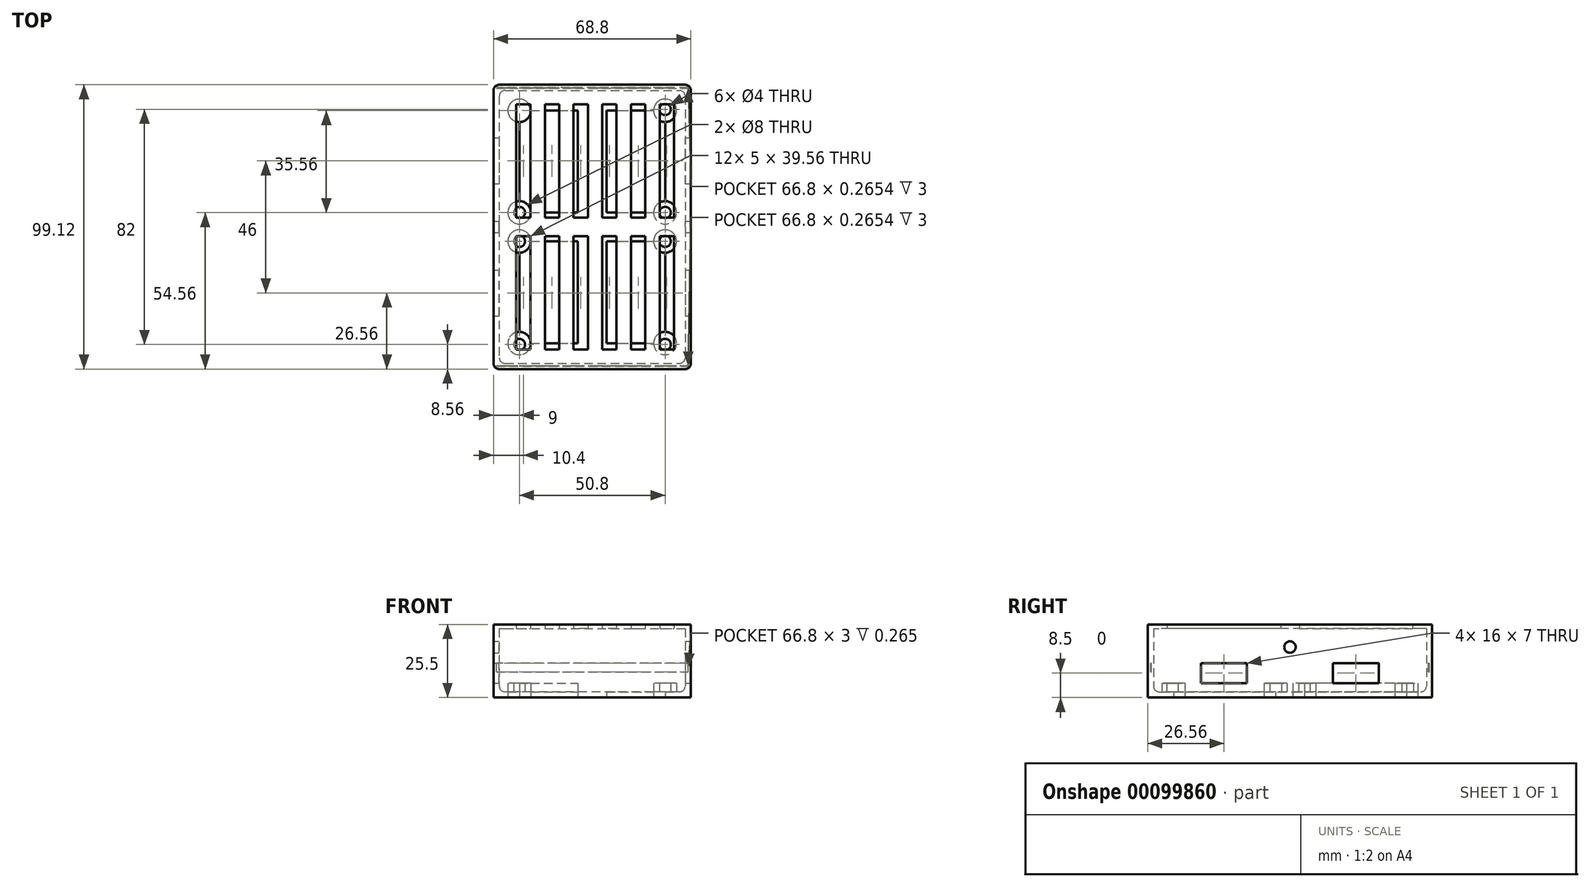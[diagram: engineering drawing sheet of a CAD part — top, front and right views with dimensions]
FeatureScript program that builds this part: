
annotation { "Feature Type Name" : "Feature", "Feature Type Description" : "" }
export const myFeature = defineFeature(function(context is Context, id is Id, definition is map)
    precondition{}
    {
        {
            var Q0;
            Q0=qCreatedBy(makeId("Top.planeOp"),FACE);
            var sketch = newSketch(context, id + "F0", { "sketchPlane" : qUnion([Q0])});
            skLineSegment(sketch, "E0.top", {"start": v(-32.4, -24.56) * mm, "end": v(32.4, -24.56) * mm});
            skLineSegment(sketch, "E0.left", {"start": v(-32.4, 24.56) * mm, "end": v(-32.4, -24.56) * mm});
            skLineSegment(sketch, "E0.right", {"start": v(32.4, 24.56) * mm, "end": v(32.4, -24.56) * mm});
            skPoint(sketch, "E0.middle", {"position": v(0, 0) * mm});
            skCircle(sketch, "E1", {"center": v(-25.4, 18) * mm, "radius": 4 * mm});
            skCircle(sketch, "E2", {"center": v(-25.4, -17.56) * mm, "radius": 4 * mm});
            skCircle(sketch, "E3", {"center": v(-25.4, 18) * mm, "radius": 2 * mm});
            skCircle(sketch, "E4", {"center": v(25.4, 18) * mm, "radius": 4 * mm});
            skCircle(sketch, "E5.MirrorC", {"center": v(-25.4, -18) * mm, "radius": 2 * mm});
            skCircle(sketch, "E6.MirrorC", {"center": v(25.4, 18) * mm, "radius": 2 * mm});
            skCircle(sketch, "E7.MirrorC", {"center": v(25.4, -18) * mm, "radius": 2 * mm});
            skCircle(sketch, "E8.MirrorC", {"center": v(25.4, -17.56) * mm, "radius": 4 * mm});
            skLineSegment(sketch, "E9.top", {"start": v(-34.4, -26.56) * mm, "end": v(34.4, -26.56) * mm});
            skLineSegment(sketch, "E9.left", {"start": v(-34.4, 26.56) * mm, "end": v(-34.4, -26.56) * mm});
            skLineSegment(sketch, "E9.right", {"start": v(34.4, 26.56) * mm, "end": v(34.4, -26.56) * mm});
            skLineSegment(sketch, "E10.bottom", {"start": v(-31, 23) * mm, "end": v(31, 23) * mm, "construction": true});
            skLineSegment(sketch, "E10.top", {"start": v(-31, -23) * mm, "end": v(31, -23) * mm, "construction": true});
            skLineSegment(sketch, "E10.left", {"start": v(-31, 23) * mm, "end": v(-31, -23) * mm, "construction": true});
            skLineSegment(sketch, "E10.right", {"start": v(31, 23) * mm, "end": v(31, -23) * mm, "construction": true});
            skLineSegment(sketch, "E11.MirrorCS", {"start": v(-31, 69) * mm, "end": v(31, 69) * mm, "construction": true});
            skLineSegment(sketch, "E12", {"start": v(-31, 69) * mm, "end": v(-31, 23) * mm, "construction": true});
            skLineSegment(sketch, "E13", {"start": v(31, 69) * mm, "end": v(31, 23) * mm, "construction": true});
            skLineSegment(sketch, "E14.MirrorCS", {"start": v(-32.4, 70.56) * mm, "end": v(32.4, 70.56) * mm});
            skLineSegment(sketch, "E15.MirrorCS", {"start": v(-34.4, 72.56) * mm, "end": v(34.4, 72.56) * mm});
            skLineSegment(sketch, "E16", {"start": v(-32.4, 70.56) * mm, "end": v(-32.4, 24.56) * mm});
            skLineSegment(sketch, "E17", {"start": v(-34.4, 26.56) * mm, "end": v(-34.4, 72.56) * mm});
            skLineSegment(sketch, "E18", {"start": v(32.4, 24.56) * mm, "end": v(32.4, 70.56) * mm});
            skLineSegment(sketch, "E19", {"start": v(34.4, 72.56) * mm, "end": v(34.4, 26.56) * mm});
            skCircle(sketch, "E20.MirrorC", {"center": v(-25.4, 28) * mm, "radius": 2 * mm});
            skCircle(sketch, "E21.MirrorC", {"center": v(-25.4, 28) * mm, "radius": 4 * mm});
            skCircle(sketch, "E22.MirrorC", {"center": v(25.4, 28) * mm, "radius": 2 * mm});
            skCircle(sketch, "E23.MirrorC", {"center": v(25.4, 28) * mm, "radius": 4 * mm});
            skCircle(sketch, "E24.MirrorC", {"center": v(25.4, 63.56) * mm, "radius": 4 * mm});
            skCircle(sketch, "E25.MirrorC", {"center": v(25.4, 64) * mm, "radius": 2 * mm});
            skCircle(sketch, "E26.MirrorC", {"center": v(-25.4, 63.56) * mm, "radius": 4 * mm});
            skCircle(sketch, "E27.MirrorC", {"center": v(-25.4, 64) * mm, "radius": 2 * mm});
            skLineSegment(sketch, "E28.bottom", {"start": v(-25.4, 59.56) * mm, "end": v(25.4, 59.56) * mm, "construction": true});
            skLineSegment(sketch, "E28.top", {"start": v(-25.4, -13.56) * mm, "end": v(25.4, -13.56) * mm, "construction": true});
            skLineSegment(sketch, "E28.left", {"start": v(-25.4, 59.56) * mm, "end": v(-25.4, -13.56) * mm, "construction": true});
            skLineSegment(sketch, "E28.right", {"start": v(25.4, 59.56) * mm, "end": v(25.4, -13.56) * mm, "construction": true});
            skPoint(sketch, "E29", {"position": v(0, 23) * mm});
            skLineSegment(sketch, "E30.bottom", {"start": v(-25.4, 28) * mm, "end": v(-23.4, 28) * mm});
            skLineSegment(sketch, "E30.top", {"start": v(-25.4, 18) * mm, "end": v(-5, 18) * mm});
            skLineSegment(sketch, "E30.left", {"start": v(-25.4, 28) * mm, "end": v(-25.4, 18) * mm});
            skLineSegment(sketch, "E30.right", {"start": v(25.4, 28) * mm, "end": v(25.4, 18) * mm});
            skLineSegment(sketch, "E31.bottom", {"start": v(-25.4, 63.56) * mm, "end": v(-5, 63.56) * mm});
            skLineSegment(sketch, "E31.top", {"start": v(-25.4, -17.56) * mm, "end": v(-5, -17.56) * mm});
            skLineSegment(sketch, "E31.left", {"start": v(-25.4, 63.56) * mm, "end": v(-25.4, 32) * mm});
            skLineSegment(sketch, "E31.right", {"start": v(25.4, 63.56) * mm, "end": v(25.4, -17.56) * mm});
            skLineSegment(sketch, "E32.left", {"start": v(-5, 63.56) * mm, "end": v(-5, 28) * mm});
            skLineSegment(sketch, "E32.right", {"start": v(5, 63.56) * mm, "end": v(5, 28) * mm});
            skLineSegment(sketch, "E33.trimOffspring", {"start": v(5, 63.56) * mm, "end": v(25.4, 63.56) * mm});
            skLineSegment(sketch, "E34.trimOffspring", {"start": v(5, 28) * mm, "end": v(25.4, 28) * mm});
            skLineSegment(sketch, "E35.trimOffspring", {"start": v(-5, 18) * mm, "end": v(-5, -17.56) * mm});
            skLineSegment(sketch, "E36.trimOffspring", {"start": v(5, 18) * mm, "end": v(5, -17.56) * mm});
            skLineSegment(sketch, "E37.trimOffspring", {"start": v(5, 18) * mm, "end": v(25.4, 18) * mm});
            skLineSegment(sketch, "E38.trimOffspring", {"start": v(5, -17.56) * mm, "end": v(25.4, -17.56) * mm});
            skLineSegment(sketch, "E39.trimOffspring", {"start": v(-25.4, 28) * mm, "end": v(-25.4, -17.56) * mm});
            skLineSegment(sketch, "E40.trimOffspring", {"start": v(-21.4, 28) * mm, "end": v(-5, 28) * mm});
            skSolve(sketch);
        }
        {
            var Q0;
            Q0 = qSketchRegion(id + "F0", true);
            var Q1;
            Q1=makeQuery(id+"F0.imprint","IMPRINT",FACE,{"disambiguationData":[TD([[makeQuery(id+"F0.imprint","IMPRINT",EDGE,{"derivedFrom":sQuery(id+"F0.wireOp",EDGE,"E0.top")}),1.0]])]});
            extrude(context, id + "F1", {"entities" : qUnion([Q0, Q1]), "depth" : 2 * mm});
        }
        {
            var Q0;
            Q0=makeQuery(id+"F0.imprint","IMPRINT",FACE,{"disambiguationData":[TD([[makeQuery(id+"F0.imprint","IMPRINT",EDGE,{"derivedFrom":sQuery(id+"F0.wireOp",EDGE,"E1")}),1.0]])]});
            var Q1;
            Q1=makeQuery(id+"F0.imprint","IMPRINT",FACE,{"disambiguationData":[TD([[makeQuery(id+"F0.imprint","IMPRINT",EDGE,{"derivedFrom":sQuery(id+"F0.wireOp",EDGE,"E4")}),1.0]])]});
            var Q2;
            Q2=makeQuery(id+"F0.imprint","IMPRINT",FACE,{"disambiguationData":[TD([[makeQuery(id+"F0.imprint","IMPRINT",EDGE,{"derivedFrom":sQuery(id+"F0.wireOp",EDGE,"E7.MirrorC")}),-1.0]])]});
            var Q3;
            Q3=makeQuery(id+"F0.imprint","IMPRINT",FACE,{"disambiguationData":[TD([[makeQuery(id+"F0.imprint","IMPRINT",EDGE,{"derivedFrom":sQuery(id+"F0.wireOp",EDGE,"E2")}),1.0]])]});
            var Q4;
            Q4=makeQuery(id+"F0.imprint","IMPRINT",FACE,{"disambiguationData":[TD([[makeQuery(id+"F0.imprint","IMPRINT",EDGE,{"derivedFrom":sQuery(id+"F0.wireOp",EDGE,"E20.MirrorC")}),1.0]])]});
            var Q5;
            Q5=makeQuery(id+"F0.imprint","IMPRINT",FACE,{"disambiguationData":[TD([[makeQuery(id+"F0.imprint","IMPRINT",EDGE,{"derivedFrom":sQuery(id+"F0.wireOp",EDGE,"E26.MirrorC")}),-1.0]])]});
            var Q6;
            Q6=makeQuery(id+"F0.imprint","IMPRINT",FACE,{"disambiguationData":[TD([[makeQuery(id+"F0.imprint","IMPRINT",EDGE,{"derivedFrom":sQuery(id+"F0.wireOp",EDGE,"E24.MirrorC")}),1.0]])]});
            var Q7;
            Q7=makeQuery(id+"F0.imprint","IMPRINT",FACE,{"disambiguationData":[TD([[makeQuery(id+"F0.imprint","IMPRINT",EDGE,{"derivedFrom":sQuery(id+"F0.wireOp",EDGE,"E22.MirrorC")}),-1.0]])]});
            extrude(context, id + "F2", {"entities" : qUnion([Q0, Q1, Q2, Q3, Q4, Q5, Q6, Q7]), "operationType" : NewBodyOperationType.ADD, "depth" : 5 * mm});
        }
        {
            var Q0;
            Q0=makeQuery(id+"F0.imprint","IMPRINT",FACE,{"disambiguationData":[TD([[makeQuery(id+"F0.imprint","IMPRINT",EDGE,{"derivedFrom":sQuery(id+"F0.wireOp",EDGE,"E0.top")}),-1.0]])]});
            extrude(context, id + "F3", {"entities" : qUnion([Q0]), "operationType" : NewBodyOperationType.ADD, "depth" : 12 * mm});
        }
        {
            var Q0;
            Q0=makeQuery(id+"F3.opExtrude","CAP_FACE",FACE,{"disambiguationData":[OSD([sQuery(id+"F0.wireOp",EDGE,"E0.bottom"),sQuery(id+"F0.wireOp",EDGE,"E0.top"),sQuery(id+"F0.wireOp",EDGE,"E0.left"),sQuery(id+"F0.wireOp",EDGE,"E0.right"),sQuery(id+"F0.wireOp",EDGE,"E9.bottom"),sQuery(id+"F0.wireOp",EDGE,"E9.top"),sQuery(id+"F0.wireOp",EDGE,"E9.left"),sQuery(id+"F0.wireOp",EDGE,"E9.right")])],"isStart":false});
            var sketch = newSketch(context, id + "F4", { "sketchPlane" : qUnion([Q0])});
            skLineSegment(sketch, "E41.top", {"start": v(-33.4, -25.3) * mm, "end": v(33.4, -25.3) * mm});
            skLineSegment(sketch, "E41.left", {"start": v(-33.4, 25.3) * mm, "end": v(-33.4, -25.3) * mm});
            skLineSegment(sketch, "E41.right", {"start": v(33.4, 25.3) * mm, "end": v(33.4, -25.3) * mm});
            skPoint(sketch, "E41.middle", {"position": v(0, 0) * mm});
            skLineSegment(sketch, "E42.0", {"start": v(-34.4, -26.56) * mm, "end": v(-34.4, -26.56) * mm});
            skLineSegment(sketch, "E43.0", {"start": v(-34.4, -26.56) * mm, "end": v(34.4, -26.56) * mm});
            skLineSegment(sketch, "E44.0", {"start": v(34.4, -26.56) * mm, "end": v(34.4, -26.56) * mm});
            skLineSegment(sketch, "E45.0", {"start": v(-31, 23) * mm, "end": v(31, 23) * mm, "construction": true});
            skLineSegment(sketch, "E46.MirrorCS", {"start": v(-33.4, 71.3) * mm, "end": v(33.4, 71.3) * mm});
            skLineSegment(sketch, "E47.MirrorCS", {"start": v(-34.4, 72.56) * mm, "end": v(34.4, 72.56) * mm});
            skLineSegment(sketch, "E48.MirrorCS", {"start": v(33.4, 20.7) * mm, "end": v(33.4, 71.3) * mm});
            skLineSegment(sketch, "E49.MirrorCS", {"start": v(-33.4, 20.7) * mm, "end": v(-33.4, 71.3) * mm});
            skLineSegment(sketch, "E50.0", {"start": v(-34.4, 26.56) * mm, "end": v(-34.4, 72.56) * mm});
            skLineSegment(sketch, "E51.0", {"start": v(-34.4, 26.56) * mm, "end": v(-34.4, -26.56) * mm});
            skLineSegment(sketch, "E52.0", {"start": v(34.4, 72.56) * mm, "end": v(34.4, 26.56) * mm});
            skLineSegment(sketch, "E53.0", {"start": v(34.4, 26.56) * mm, "end": v(34.4, -26.56) * mm});
            skPoint(sketch, "E54.MirrorCS.end.orphan", {"position": v(30.4, 68.78) * mm});
            skPoint(sketch, "E54.MirrorCS.start.orphan", {"position": v(-30.4, 68.78) * mm});
            skPoint(sketch, "E55.MirrorCS.start.orphan", {"position": v(-30.4, 23.22) * mm});
            skPoint(sketch, "E56.0.1.start.orphan", {"position": v(-30.4, 22.78) * mm});
            skPoint(sketch, "E56.0.2.start.orphan", {"position": v(-30.4, -22.78) * mm});
            skPoint(sketch, "E56.0.3.end.orphan", {"position": v(30.4, 22.78) * mm});
            skPoint(sketch, "E56.0.3.start.orphan", {"position": v(30.4, -22.78) * mm});
            skPoint(sketch, "E57.MirrorCS.end.orphan", {"position": v(30.4, 23.22) * mm});
            skSolve(sketch);
        }
        {
            var Q0;
            Q0 = qSketchRegion(id + "F4", true);
            extrude(context, id + "F5", {"entities" : qUnion([Q0]), "operationType" : NewBodyOperationType.REMOVE, "oppositeDirection" : true, "depth" : 3 * mm});
        }
        {
            var Q0;
            Q0=makeQuery(id+"F5.boolean.opBoolean","COPY",FACE,{"derivedFrom":makeQuery(id+"F5.opExtrude","CAP_FACE",FACE,{"disambiguationData":[OSD([sQuery(id+"F4.wireOp",EDGE,"E41.top"),sQuery(id+"F4.wireOp",EDGE,"E41.left"),sQuery(id+"F4.wireOp",EDGE,"E41.right"),sQuery(id+"F4.wireOp",EDGE,"E43.0"),sQuery(id+"F4.wireOp",EDGE,"E46.MirrorCS"),sQuery(id+"F4.wireOp",EDGE,"E47.MirrorCS"),sQuery(id+"F4.wireOp",EDGE,"E48.MirrorCS"),sQuery(id+"F4.wireOp",EDGE,"E49.MirrorCS"),sQuery(id+"F4.wireOp",EDGE,"E50.0"),sQuery(id+"F4.wireOp",EDGE,"E51.0"),sQuery(id+"F4.wireOp",EDGE,"E52.0"),sQuery(id+"F4.wireOp",EDGE,"E53.0")])],"isStart":false})});
            cPlane(context, id + "F6", {"entities" : qUnion([Q0]), "cplaneType" : CPlaneType.OFFSET, "offset" : 15 * mm, "width" : 150 * mm, "height" : 150 * mm});
        }
        {
            var Q0;
            Q0=qCreatedBy(id+"F6.planeOp",FACE);
            var sketch = newSketch(context, id + "F7", { "sketchPlane" : qUnion([Q0])});
            skLineSegment(sketch, "E58.left", {"start": v(-26.5, 19.78) * mm, "end": v(-26.5, -19.78) * mm});
            skLineSegment(sketch, "E59", {"start": v(-26.5, 19.78) * mm, "end": v(-21.5, 19.78) * mm});
            skLineSegment(sketch, "E60", {"start": v(-21.5, 19.78) * mm, "end": v(-21.5, -19.78) * mm});
            skLineSegment(sketch, "E61", {"start": v(-26.5, -19.78) * mm, "end": v(-21.5, -19.78) * mm});
            skLineSegment(sketch, "E62.left", {"start": v(-16.5, 19.78) * mm, "end": v(-16.5, -19.78) * mm});
            skLineSegment(sketch, "E63", {"start": v(-16.5, 19.78) * mm, "end": v(-11.5, 19.78) * mm});
            skLineSegment(sketch, "E64", {"start": v(-11.5, 19.78) * mm, "end": v(-11.5, -19.78) * mm});
            skLineSegment(sketch, "E65", {"start": v(-16.5, -19.78) * mm, "end": v(-11.5, -19.78) * mm});
            skLineSegment(sketch, "E66", {"start": v(-9, 22.94) * mm, "end": v(-9, -17.5) * mm, "construction": true});
            skLineSegment(sketch, "E67.MirrorCS", {"start": v(8.5, 19.78) * mm, "end": v(3.5, 19.78) * mm});
            skLineSegment(sketch, "E68.MirrorCS", {"start": v(8.5, 19.78) * mm, "end": v(8.5, -19.78) * mm});
            skLineSegment(sketch, "E69.MirrorCS", {"start": v(3.5, 19.78) * mm, "end": v(3.5, -19.78) * mm});
            skLineSegment(sketch, "E70.MirrorCS", {"start": v(-1.5, 19.78) * mm, "end": v(-1.5, -19.78) * mm});
            skLineSegment(sketch, "E71.MirrorCS", {"start": v(-1.5, 19.78) * mm, "end": v(-6.5, 19.78) * mm});
            skLineSegment(sketch, "E72.MirrorCS", {"start": v(-1.5, -19.78) * mm, "end": v(-6.5, -19.78) * mm});
            skLineSegment(sketch, "E73.MirrorCS", {"start": v(8.5, -19.78) * mm, "end": v(3.5, -19.78) * mm});
            skLineSegment(sketch, "E74.MirrorCS", {"start": v(-6.5, 19.78) * mm, "end": v(-6.5, -19.78) * mm});
            skLineSegment(sketch, "E75", {"start": v(11, 21.68) * mm, "end": v(11, -19.6) * mm, "construction": true});
            skLineSegment(sketch, "E76.MirrorCS", {"start": v(23.5, 19.78) * mm, "end": v(28.5, 19.78) * mm});
            skLineSegment(sketch, "E77.MirrorCS", {"start": v(18.5, 19.78) * mm, "end": v(18.5, -19.78) * mm});
            skLineSegment(sketch, "E78.MirrorCS", {"start": v(23.5, 19.78) * mm, "end": v(23.5, -19.78) * mm});
            skLineSegment(sketch, "E79.MirrorCS", {"start": v(23.5, -19.78) * mm, "end": v(28.5, -19.78) * mm});
            skLineSegment(sketch, "E80.MirrorCS", {"start": v(13.5, -19.78) * mm, "end": v(18.5, -19.78) * mm});
            skLineSegment(sketch, "E81.MirrorCS", {"start": v(13.5, 19.78) * mm, "end": v(13.5, -19.78) * mm});
            skLineSegment(sketch, "E82.MirrorCS", {"start": v(13.5, 19.78) * mm, "end": v(18.5, 19.78) * mm});
            skLineSegment(sketch, "E83.MirrorCS", {"start": v(28.5, 19.78) * mm, "end": v(28.5, -19.78) * mm});
            skLineSegment(sketch, "E84", {"start": v(31, 21.5) * mm, "end": v(31, -15.9) * mm, "construction": true});
            skLineSegment(sketch, "E85.0", {"start": v(-32.4, -24.56) * mm, "end": v(32.4, -24.56) * mm});
            skLineSegment(sketch, "E86.0", {"start": v(-32.4, 24.56) * mm, "end": v(-32.4, -24.56) * mm});
            skLineSegment(sketch, "E87", {"start": v(32.4, -24.56) * mm, "end": v(32.4, 21) * mm});
            skLineSegment(sketch, "E88.0", {"start": v(-34.4, 26.56) * mm, "end": v(-34.4, -26.56) * mm});
            skLineSegment(sketch, "E89.0", {"start": v(34.4, 26.56) * mm, "end": v(34.4, -26.56) * mm});
            skLineSegment(sketch, "E90.0", {"start": v(-34.4, -26.56) * mm, "end": v(34.4, -26.56) * mm});
            skLineSegment(sketch, "E91.0", {"start": v(33.4, 23.78) * mm, "end": v(33.4, -25.3) * mm});
            skLineSegment(sketch, "E92.MirrorCS", {"start": v(13.5, 65.78) * mm, "end": v(18.5, 65.78) * mm});
            skLineSegment(sketch, "E93.MirrorCS", {"start": v(23.5, 26.22) * mm, "end": v(28.5, 26.22) * mm});
            skLineSegment(sketch, "E94.MirrorCS", {"start": v(13.5, 26.22) * mm, "end": v(18.5, 26.22) * mm});
            skLineSegment(sketch, "E95.MirrorCS", {"start": v(-16.5, 65.78) * mm, "end": v(-11.5, 65.78) * mm});
            skLineSegment(sketch, "E96.MirrorCS", {"start": v(-26.5, 65.78) * mm, "end": v(-21.5, 65.78) * mm});
            skLineSegment(sketch, "E97.MirrorCS", {"start": v(-1.5, 65.78) * mm, "end": v(-6.5, 65.78) * mm});
            skLineSegment(sketch, "E98.MirrorCS", {"start": v(-1.5, 26.22) * mm, "end": v(-6.5, 26.22) * mm});
            skLineSegment(sketch, "E99.MirrorCS", {"start": v(-26.5, 26.22) * mm, "end": v(-21.5, 26.22) * mm});
            skLineSegment(sketch, "E100.MirrorCS", {"start": v(8.5, 65.78) * mm, "end": v(3.5, 65.78) * mm});
            skLineSegment(sketch, "E101.MirrorCS", {"start": v(8.5, 26.22) * mm, "end": v(3.5, 26.22) * mm});
            skLineSegment(sketch, "E102.MirrorCS", {"start": v(-16.5, 26.22) * mm, "end": v(-11.5, 26.22) * mm});
            skLineSegment(sketch, "E103.MirrorCS", {"start": v(23.5, 65.78) * mm, "end": v(28.5, 65.78) * mm});
            skLineSegment(sketch, "E104.MirrorCS", {"start": v(11, 24.32) * mm, "end": v(11, 65.6) * mm, "construction": true});
            skLineSegment(sketch, "E105.MirrorCS", {"start": v(-6.5, 26.22) * mm, "end": v(-6.5, 65.78) * mm});
            skLineSegment(sketch, "E106.MirrorCS", {"start": v(23.5, 26.22) * mm, "end": v(23.5, 65.78) * mm});
            skLineSegment(sketch, "E107.MirrorCS", {"start": v(28.5, 26.22) * mm, "end": v(28.5, 65.78) * mm});
            skLineSegment(sketch, "E108.MirrorCS", {"start": v(8.5, 26.22) * mm, "end": v(8.5, 65.78) * mm});
            skLineSegment(sketch, "E109.MirrorCS", {"start": v(-1.5, 26.22) * mm, "end": v(-1.5, 65.78) * mm});
            skLineSegment(sketch, "E110.MirrorCS", {"start": v(18.5, 26.22) * mm, "end": v(18.5, 65.78) * mm});
            skLineSegment(sketch, "E111.MirrorCS", {"start": v(31, 24.5) * mm, "end": v(31, 61.9) * mm, "construction": true});
            skLineSegment(sketch, "E112.MirrorCS", {"start": v(3.5, 26.22) * mm, "end": v(3.5, 65.78) * mm});
            skLineSegment(sketch, "E113.MirrorCS", {"start": v(-26.5, 26.22) * mm, "end": v(-26.5, 65.78) * mm});
            skLineSegment(sketch, "E114.MirrorCS", {"start": v(-21.5, 26.22) * mm, "end": v(-21.5, 65.78) * mm});
            skLineSegment(sketch, "E115.MirrorCS", {"start": v(-9, 23.06) * mm, "end": v(-9, 63.5) * mm, "construction": true});
            skLineSegment(sketch, "E116.MirrorCS", {"start": v(-11.5, 26.22) * mm, "end": v(-11.5, 65.78) * mm});
            skLineSegment(sketch, "E117.MirrorCS", {"start": v(13.5, 26.22) * mm, "end": v(13.5, 65.78) * mm});
            skLineSegment(sketch, "E118.MirrorCS", {"start": v(-16.5, 26.22) * mm, "end": v(-16.5, 65.78) * mm});
            skLineSegment(sketch, "E119.MirrorCS", {"start": v(-34.4, 72.56) * mm, "end": v(34.4, 72.56) * mm});
            skLineSegment(sketch, "E120.MirrorCS", {"start": v(-34.4, 19.44) * mm, "end": v(-34.4, 72.56) * mm});
            skLineSegment(sketch, "E121.MirrorCS", {"start": v(34.4, 19.44) * mm, "end": v(34.4, 72.56) * mm});
            skPoint(sketch, "E122.0.end.orphan", {"position": v(-33.4, -25.3) * mm});
            skPoint(sketch, "E123.orphan", {"position": v(-28.4, 25.22) * mm});
            skPoint(sketch, "E124.0.start.orphan", {"position": v(-28.4, 20.78) * mm});
            skPoint(sketch, "E125.orphan", {"position": v(32.4, 25) * mm});
            skPoint(sketch, "E126.0", {"position": v(-32.4, 70.56) * mm});
            skPoint(sketch, "E127.0", {"position": v(32.4, 70.56) * mm});
            skLineSegment(sketch, "E128.bottom", {"start": v(-32.4, 70.56) * mm, "end": v(32.4, 70.56) * mm});
            skLineSegment(sketch, "E128.left", {"start": v(-32.4, 70.56) * mm, "end": v(-32.4, -24.56) * mm});
            skLineSegment(sketch, "E128.right", {"start": v(32.4, 70.56) * mm, "end": v(32.4, -24.56) * mm});
            skLineSegment(sketch, "E129.top", {"start": v(33.4, 71.56) * mm, "end": v(-33.4, 71.56) * mm});
            skLineSegment(sketch, "E129.left", {"start": v(33.4, -25.3) * mm, "end": v(33.4, 71.56) * mm});
            skLineSegment(sketch, "E129.right", {"start": v(-33.4, -25.3) * mm, "end": v(-33.4, 71.56) * mm});
            skLineSegment(sketch, "E130", {"start": v(-33.4, -25.56) * mm, "end": v(33.4, -25.56) * mm});
            skLineSegment(sketch, "E131", {"start": v(33.4, -25.56) * mm, "end": v(33.4, -25.3) * mm});
            skLineSegment(sketch, "E132", {"start": v(-33.4, -25.3) * mm, "end": v(-33.4, -25.56) * mm});
            skPoint(sketch, "E133.orphan", {"position": v(33.5, 19.78) * mm});
            skPoint(sketch, "E134.MirrorCS.end.orphan", {"position": v(33.5, -19.78) * mm});
            skPoint(sketch, "E135.MirrorCS.start.orphan", {"position": v(33.5, 26.22) * mm});
            skPoint(sketch, "E136.orphan", {"position": v(33.5, 65.78) * mm});
            skPoint(sketch, "E137.MirrorCS.start.orphan", {"position": v(38.5, 65.78) * mm});
            skSolve(sketch);
        }
        {
            var Q0;
            Q0=makeQuery(id+"F7.imprint","IMPRINT",FACE,{"disambiguationData":[TD([[makeQuery(id+"F7.imprint","IMPRINT",EDGE,{"derivedFrom":sQuery(id+"F7.wireOp",EDGE,"E58.left")}),-1.0]])]});
            var Q1;
            {var subQ7=sQuery(id+"F7.wireOp",EDGE,"E128.bottom");Q1=makeQuery(id+"F7.imprint","IMPRINT",FACE,{"disambiguationData":[TD([[makeQuery(id+"F7.imprint","IMPRINT",EDGE,{"derivedFrom":subQ7}),1.0]])]});}
            var Q2;
            {var subQ8=sQuery(id+"F7.wireOp",EDGE,"E88.0");Q2=makeQuery(id+"F7.imprint","IMPRINT",FACE,{"disambiguationData":[TD([[makeQuery(id+"F7.imprint","IMPRINT",EDGE,{"derivedFrom":subQ8}),1.0]])]});}
            extrude(context, id + "F8", {"entities" : qUnion([Q0, Q1, Q2]), "depth" : 1.5 * mm});
        }
        {
            var Q0;
            Q0 = qSketchRegion(id + "F7", true);
            extrude(context, id + "F9", {"entities" : qUnion([Q0]), "operationType" : NewBodyOperationType.ADD, "oppositeDirection" : true, "depth" : 15 * mm});
        }
        {
            var Q0;
            {var subQ7=sQuery(id+"F7.wireOp",EDGE,"E128.bottom");Q0=makeQuery(id+"F7.imprint","IMPRINT",FACE,{"disambiguationData":[TD([[makeQuery(id+"F7.imprint","IMPRINT",EDGE,{"derivedFrom":subQ7}),1.0]])]});}
            extrude(context, id + "F10", {"entities" : qUnion([Q0]), "operationType" : NewBodyOperationType.ADD, "oppositeDirection" : true, "depth" : 12 * mm});
        }
        {
            var Q0;
            Q0=qCreatedBy(makeId("Right.planeOp"),FACE);
            var sketch = newSketch(context, id + "F11", { "sketchPlane" : qUnion([Q0])});
            skLineSegment(sketch, "E138.bottom", {"start": v(-8, 5) * mm, "end": v(8, 5) * mm});
            skLineSegment(sketch, "E138.top", {"start": v(-8, 12) * mm, "end": v(8, 12) * mm});
            skLineSegment(sketch, "E138.left", {"start": v(-8, 5) * mm, "end": v(-8, 12) * mm});
            skLineSegment(sketch, "E138.right", {"start": v(8, 5) * mm, "end": v(8, 12) * mm});
            skPoint(sketch, "E139.0", {"position": v(23, 0) * mm});
            skLineSegment(sketch, "E140", {"start": v(23, 0) * mm, "end": v(23, 28.63) * mm, "construction": true});
            skLineSegment(sketch, "E141.MirrorCS", {"start": v(38, 5) * mm, "end": v(38, 12) * mm});
            skLineSegment(sketch, "E142.MirrorCS", {"start": v(54, 12) * mm, "end": v(38, 12) * mm});
            skLineSegment(sketch, "E143.MirrorCS", {"start": v(54, 5) * mm, "end": v(38, 5) * mm});
            skLineSegment(sketch, "E144.MirrorCS", {"start": v(54, 5) * mm, "end": v(54, 12) * mm});
            skLineSegment(sketch, "E145", {"start": v(23, 26.11) * mm, "end": v(23, 9.1) * mm, "construction": true});
            skCircle(sketch, "E146", {"center": v(23, 17.6) * mm, "radius": 2 * mm});
            skSolve(sketch);
        }
        {
            var Q0;
            Q0 = qSketchRegion(id + "F11", true);
            extrude(context, id + "F12", {"entities" : qUnion([Q0]), "operationType" : NewBodyOperationType.REMOVE, "oppositeDirection" : true, "depth" : 40 * mm, "hasSecondDirection" : true, "secondDirectionOppositeDirection" : false, "secondDirectionDepth" : 40 * mm});
        }
        {
            var Q0;
            Q0=makeQuery(id+"F3.boolean.opBoolean","INTERSECT",EDGE,{"derivedFrom":[makeQuery(id+"F1.opExtrude","CAP_FACE",FACE,{"disambiguationData":[OSD([sQuery(id+"F0.wireOp",EDGE,"E1"),sQuery(id+"F0.wireOp",EDGE,"E2"),sQuery(id+"F0.wireOp",EDGE,"E4"),sQuery(id+"F0.wireOp",EDGE,"E8.MirrorC"),sQuery(id+"F0.wireOp",EDGE,"E9.top"),sQuery(id+"F0.wireOp",EDGE,"E9.left"),sQuery(id+"F0.wireOp",EDGE,"E9.right"),sQuery(id+"F0.wireOp",EDGE,"E15.MirrorCS"),sQuery(id+"F0.wireOp",EDGE,"E17"),sQuery(id+"F0.wireOp",EDGE,"E19"),sQuery(id+"F0.wireOp",EDGE,"E21.MirrorC"),sQuery(id+"F0.wireOp",EDGE,"E23.MirrorC"),sQuery(id+"F0.wireOp",EDGE,"E24.MirrorC"),sQuery(id+"F0.wireOp",EDGE,"E26.MirrorC"),sQuery(id+"F0.wireOp",EDGE,"Y289rVv9-n25F-z0Kw-bMLE-9brTHhUNfFZQ.bottom"),sQuery(id+"F0.wireOp",EDGE,"Y289rVv9-n25F-z0Kw-bMLE-9brTHhUNfFZQ.top"),sQuery(id+"F0.wireOp",EDGE,"Y289rVv9-n25F-z0Kw-bMLE-9brTHhUNfFZQ.left"),sQuery(id+"F0.wireOp",EDGE,"4SwM954j-JW78-bTZh-loK3-HON2JweZRsLD.left"),sQuery(id+"F0.wireOp",EDGE,"tZNsfNJw-30fH-ebqf-lx2E-8Ruw7eE0hOgg.left"),sQuery(id+"F0.wireOp",EDGE,"8919tPv0-7Dmb-Q3s9-tR7e-7PeE0iw5I7E1.left"),sQuery(id+"F0.wireOp",EDGE,"135003fa-3c42-477e-a3b7-4dc5e2bd5861.trimOffspring"),sQuery(id+"F0.wireOp",EDGE,"19a097cc-b49c-4f54-a7c1-ecc35be2ba40.trimOffspring"),sQuery(id+"F0.wireOp",EDGE,"a2873cc1-fee8-4c2c-8ffd-20262f109c54.trimOffspring"),sQuery(id+"F0.wireOp",EDGE,"7d6903a8-e306-4b0e-84cb-2cc0841f7eb70.MirrorCS"),sQuery(id+"F0.wireOp",EDGE,"c135d9d7-46c4-4e0c-b929-17f007d6f2950.MirrorCS"),sQuery(id+"F0.wireOp",EDGE,"a26210e0-8e15-423a-9de0-b08072d058db0.MirrorCS"),sQuery(id+"F0.wireOp",EDGE,"95b8c553-0250-4fa0-9f86-d06bdbb85b1b0.MirrorCS"),sQuery(id+"F0.wireOp",EDGE,"c4420f40-08eb-417d-8682-3f3f4c26891a.trimOffspring"),sQuery(id+"F0.wireOp",EDGE,"64571030-5dd4-4b7f-bd83-8db9fa176ad0.trimOffspring"),sQuery(id+"F0.wireOp",EDGE,"1kqOLQRp-1IiC-if5W-8HwA-EEcHAn70aZ6N")])],"isStart":false}),makeQuery(id+"F3.opExtrude","SWEPT_FACE",FACE,{"disambiguationData":[OSD([sQuery(id+"F0.wireOp",EDGE,"E14.MirrorCS")])]})]});
            var Q1;
            Q1=makeQuery(id+"F3.boolean.opBoolean","INTERSECT",EDGE,{"derivedFrom":[makeQuery(id+"F1.opExtrude","CAP_FACE",FACE,{"disambiguationData":[OSD([sQuery(id+"F0.wireOp",EDGE,"E1"),sQuery(id+"F0.wireOp",EDGE,"E2"),sQuery(id+"F0.wireOp",EDGE,"E4"),sQuery(id+"F0.wireOp",EDGE,"E8.MirrorC"),sQuery(id+"F0.wireOp",EDGE,"E9.top"),sQuery(id+"F0.wireOp",EDGE,"E9.left"),sQuery(id+"F0.wireOp",EDGE,"E9.right"),sQuery(id+"F0.wireOp",EDGE,"E15.MirrorCS"),sQuery(id+"F0.wireOp",EDGE,"E17"),sQuery(id+"F0.wireOp",EDGE,"E19"),sQuery(id+"F0.wireOp",EDGE,"E21.MirrorC"),sQuery(id+"F0.wireOp",EDGE,"E23.MirrorC"),sQuery(id+"F0.wireOp",EDGE,"E24.MirrorC"),sQuery(id+"F0.wireOp",EDGE,"E26.MirrorC"),sQuery(id+"F0.wireOp",EDGE,"Y289rVv9-n25F-z0Kw-bMLE-9brTHhUNfFZQ.bottom"),sQuery(id+"F0.wireOp",EDGE,"Y289rVv9-n25F-z0Kw-bMLE-9brTHhUNfFZQ.top"),sQuery(id+"F0.wireOp",EDGE,"Y289rVv9-n25F-z0Kw-bMLE-9brTHhUNfFZQ.left"),sQuery(id+"F0.wireOp",EDGE,"4SwM954j-JW78-bTZh-loK3-HON2JweZRsLD.left"),sQuery(id+"F0.wireOp",EDGE,"tZNsfNJw-30fH-ebqf-lx2E-8Ruw7eE0hOgg.left"),sQuery(id+"F0.wireOp",EDGE,"8919tPv0-7Dmb-Q3s9-tR7e-7PeE0iw5I7E1.left"),sQuery(id+"F0.wireOp",EDGE,"135003fa-3c42-477e-a3b7-4dc5e2bd5861.trimOffspring"),sQuery(id+"F0.wireOp",EDGE,"19a097cc-b49c-4f54-a7c1-ecc35be2ba40.trimOffspring"),sQuery(id+"F0.wireOp",EDGE,"a2873cc1-fee8-4c2c-8ffd-20262f109c54.trimOffspring"),sQuery(id+"F0.wireOp",EDGE,"7d6903a8-e306-4b0e-84cb-2cc0841f7eb70.MirrorCS"),sQuery(id+"F0.wireOp",EDGE,"c135d9d7-46c4-4e0c-b929-17f007d6f2950.MirrorCS"),sQuery(id+"F0.wireOp",EDGE,"a26210e0-8e15-423a-9de0-b08072d058db0.MirrorCS"),sQuery(id+"F0.wireOp",EDGE,"95b8c553-0250-4fa0-9f86-d06bdbb85b1b0.MirrorCS"),sQuery(id+"F0.wireOp",EDGE,"c4420f40-08eb-417d-8682-3f3f4c26891a.trimOffspring"),sQuery(id+"F0.wireOp",EDGE,"64571030-5dd4-4b7f-bd83-8db9fa176ad0.trimOffspring"),sQuery(id+"F0.wireOp",EDGE,"1kqOLQRp-1IiC-if5W-8HwA-EEcHAn70aZ6N")])],"isStart":false}),makeQuery(id+"F3.opExtrude","SWEPT_FACE",FACE,{"disambiguationData":[OSD([sQuery(id+"F0.wireOp",EDGE,"E0.left"),sQuery(id+"F0.wireOp",EDGE,"E16")])]})]});
            var Q2;
            Q2=makeQuery(id+"F3.boolean.opBoolean","INTERSECT",EDGE,{"derivedFrom":[makeQuery(id+"F1.opExtrude","CAP_FACE",FACE,{"disambiguationData":[OSD([sQuery(id+"F0.wireOp",EDGE,"E1"),sQuery(id+"F0.wireOp",EDGE,"E2"),sQuery(id+"F0.wireOp",EDGE,"E4"),sQuery(id+"F0.wireOp",EDGE,"E8.MirrorC"),sQuery(id+"F0.wireOp",EDGE,"E9.top"),sQuery(id+"F0.wireOp",EDGE,"E9.left"),sQuery(id+"F0.wireOp",EDGE,"E9.right"),sQuery(id+"F0.wireOp",EDGE,"E15.MirrorCS"),sQuery(id+"F0.wireOp",EDGE,"E17"),sQuery(id+"F0.wireOp",EDGE,"E19"),sQuery(id+"F0.wireOp",EDGE,"E21.MirrorC"),sQuery(id+"F0.wireOp",EDGE,"E23.MirrorC"),sQuery(id+"F0.wireOp",EDGE,"E24.MirrorC"),sQuery(id+"F0.wireOp",EDGE,"E26.MirrorC"),sQuery(id+"F0.wireOp",EDGE,"Y289rVv9-n25F-z0Kw-bMLE-9brTHhUNfFZQ.bottom"),sQuery(id+"F0.wireOp",EDGE,"Y289rVv9-n25F-z0Kw-bMLE-9brTHhUNfFZQ.top"),sQuery(id+"F0.wireOp",EDGE,"Y289rVv9-n25F-z0Kw-bMLE-9brTHhUNfFZQ.left"),sQuery(id+"F0.wireOp",EDGE,"4SwM954j-JW78-bTZh-loK3-HON2JweZRsLD.left"),sQuery(id+"F0.wireOp",EDGE,"tZNsfNJw-30fH-ebqf-lx2E-8Ruw7eE0hOgg.left"),sQuery(id+"F0.wireOp",EDGE,"8919tPv0-7Dmb-Q3s9-tR7e-7PeE0iw5I7E1.left"),sQuery(id+"F0.wireOp",EDGE,"135003fa-3c42-477e-a3b7-4dc5e2bd5861.trimOffspring"),sQuery(id+"F0.wireOp",EDGE,"19a097cc-b49c-4f54-a7c1-ecc35be2ba40.trimOffspring"),sQuery(id+"F0.wireOp",EDGE,"a2873cc1-fee8-4c2c-8ffd-20262f109c54.trimOffspring"),sQuery(id+"F0.wireOp",EDGE,"7d6903a8-e306-4b0e-84cb-2cc0841f7eb70.MirrorCS"),sQuery(id+"F0.wireOp",EDGE,"c135d9d7-46c4-4e0c-b929-17f007d6f2950.MirrorCS"),sQuery(id+"F0.wireOp",EDGE,"a26210e0-8e15-423a-9de0-b08072d058db0.MirrorCS"),sQuery(id+"F0.wireOp",EDGE,"95b8c553-0250-4fa0-9f86-d06bdbb85b1b0.MirrorCS"),sQuery(id+"F0.wireOp",EDGE,"c4420f40-08eb-417d-8682-3f3f4c26891a.trimOffspring"),sQuery(id+"F0.wireOp",EDGE,"64571030-5dd4-4b7f-bd83-8db9fa176ad0.trimOffspring"),sQuery(id+"F0.wireOp",EDGE,"1kqOLQRp-1IiC-if5W-8HwA-EEcHAn70aZ6N")])],"isStart":false}),makeQuery(id+"F3.opExtrude","SWEPT_FACE",FACE,{"disambiguationData":[OSD([sQuery(id+"F0.wireOp",EDGE,"E0.right"),sQuery(id+"F0.wireOp",EDGE,"E18")])]})]});
            var Q3;
            Q3=makeQuery(id+"F3.boolean.opBoolean","INTERSECT",EDGE,{"derivedFrom":[makeQuery(id+"F1.opExtrude","CAP_FACE",FACE,{"disambiguationData":[OSD([sQuery(id+"F0.wireOp",EDGE,"E1"),sQuery(id+"F0.wireOp",EDGE,"E2"),sQuery(id+"F0.wireOp",EDGE,"E4"),sQuery(id+"F0.wireOp",EDGE,"E8.MirrorC"),sQuery(id+"F0.wireOp",EDGE,"E9.top"),sQuery(id+"F0.wireOp",EDGE,"E9.left"),sQuery(id+"F0.wireOp",EDGE,"E9.right"),sQuery(id+"F0.wireOp",EDGE,"E15.MirrorCS"),sQuery(id+"F0.wireOp",EDGE,"E17"),sQuery(id+"F0.wireOp",EDGE,"E19"),sQuery(id+"F0.wireOp",EDGE,"E21.MirrorC"),sQuery(id+"F0.wireOp",EDGE,"E23.MirrorC"),sQuery(id+"F0.wireOp",EDGE,"E24.MirrorC"),sQuery(id+"F0.wireOp",EDGE,"E26.MirrorC"),sQuery(id+"F0.wireOp",EDGE,"Y289rVv9-n25F-z0Kw-bMLE-9brTHhUNfFZQ.bottom"),sQuery(id+"F0.wireOp",EDGE,"Y289rVv9-n25F-z0Kw-bMLE-9brTHhUNfFZQ.top"),sQuery(id+"F0.wireOp",EDGE,"Y289rVv9-n25F-z0Kw-bMLE-9brTHhUNfFZQ.left"),sQuery(id+"F0.wireOp",EDGE,"4SwM954j-JW78-bTZh-loK3-HON2JweZRsLD.left"),sQuery(id+"F0.wireOp",EDGE,"tZNsfNJw-30fH-ebqf-lx2E-8Ruw7eE0hOgg.left"),sQuery(id+"F0.wireOp",EDGE,"8919tPv0-7Dmb-Q3s9-tR7e-7PeE0iw5I7E1.left"),sQuery(id+"F0.wireOp",EDGE,"135003fa-3c42-477e-a3b7-4dc5e2bd5861.trimOffspring"),sQuery(id+"F0.wireOp",EDGE,"19a097cc-b49c-4f54-a7c1-ecc35be2ba40.trimOffspring"),sQuery(id+"F0.wireOp",EDGE,"a2873cc1-fee8-4c2c-8ffd-20262f109c54.trimOffspring"),sQuery(id+"F0.wireOp",EDGE,"7d6903a8-e306-4b0e-84cb-2cc0841f7eb70.MirrorCS"),sQuery(id+"F0.wireOp",EDGE,"c135d9d7-46c4-4e0c-b929-17f007d6f2950.MirrorCS"),sQuery(id+"F0.wireOp",EDGE,"a26210e0-8e15-423a-9de0-b08072d058db0.MirrorCS"),sQuery(id+"F0.wireOp",EDGE,"95b8c553-0250-4fa0-9f86-d06bdbb85b1b0.MirrorCS"),sQuery(id+"F0.wireOp",EDGE,"c4420f40-08eb-417d-8682-3f3f4c26891a.trimOffspring"),sQuery(id+"F0.wireOp",EDGE,"64571030-5dd4-4b7f-bd83-8db9fa176ad0.trimOffspring"),sQuery(id+"F0.wireOp",EDGE,"1kqOLQRp-1IiC-if5W-8HwA-EEcHAn70aZ6N")])],"isStart":false}),makeQuery(id+"F3.opExtrude","SWEPT_FACE",FACE,{"disambiguationData":[OSD([sQuery(id+"F0.wireOp",EDGE,"E0.top")])]})]});
            var Q4;
            {var subQ0=sQuery(id+"F0.wireOp",EDGE,"E9.right");var subQ1=sQuery(id+"F0.wireOp",EDGE,"E9.top");Q4=makeQuery(id+"F3.boolean.opBoolean","MERGE",EDGE,{"derivedFrom":[makeQuery(id+"F1.opExtrude","SWEPT_EDGE",EDGE,{"disambiguationData":[OSD([subQ1,subQ0])]}),makeQuery(id+"F3.opExtrude","SWEPT_EDGE",EDGE,{"disambiguationData":[OSD([subQ1,subQ0])]})]});}
            var Q5;
            {var subQ0=sQuery(id+"F0.wireOp",EDGE,"E9.left");var subQ1=sQuery(id+"F0.wireOp",EDGE,"E9.top");Q5=makeQuery(id+"F3.boolean.opBoolean","MERGE",EDGE,{"derivedFrom":[makeQuery(id+"F1.opExtrude","SWEPT_EDGE",EDGE,{"disambiguationData":[OSD([subQ1,subQ0])]}),makeQuery(id+"F3.opExtrude","SWEPT_EDGE",EDGE,{"disambiguationData":[OSD([subQ1,subQ0])]})]});}
            var Q6;
            {var subQ0=sQuery(id+"F0.wireOp",EDGE,"E17");var subQ1=sQuery(id+"F0.wireOp",EDGE,"E15.MirrorCS");Q6=makeQuery(id+"F3.boolean.opBoolean","MERGE",EDGE,{"derivedFrom":[makeQuery(id+"F1.opExtrude","SWEPT_EDGE",EDGE,{"disambiguationData":[OSD([subQ1,subQ0])]}),makeQuery(id+"F3.opExtrude","SWEPT_EDGE",EDGE,{"disambiguationData":[OSD([subQ1,subQ0])]})]});}
            var Q7;
            {var subQ0=sQuery(id+"F0.wireOp",EDGE,"E19");var subQ1=sQuery(id+"F0.wireOp",EDGE,"E15.MirrorCS");Q7=makeQuery(id+"F3.boolean.opBoolean","MERGE",EDGE,{"derivedFrom":[makeQuery(id+"F1.opExtrude","SWEPT_EDGE",EDGE,{"disambiguationData":[OSD([subQ1,subQ0])]}),makeQuery(id+"F3.opExtrude","SWEPT_EDGE",EDGE,{"disambiguationData":[OSD([subQ1,subQ0])]})]});}
            var Q8;
            Q8=makeQuery(id+"F3.opExtrude","SWEPT_EDGE",EDGE,{"disambiguationData":[OSD([sQuery(id+"F0.wireOp",EDGE,"E14.MirrorCS"),sQuery(id+"F0.wireOp",EDGE,"E16")])]});
            var Q9;
            Q9=makeQuery(id+"F3.opExtrude","SWEPT_EDGE",EDGE,{"disambiguationData":[OSD([sQuery(id+"F0.wireOp",EDGE,"E14.MirrorCS"),sQuery(id+"F0.wireOp",EDGE,"E18")])]});
            var Q10;
            Q10=makeQuery(id+"F3.opExtrude","SWEPT_EDGE",EDGE,{"disambiguationData":[OSD([sQuery(id+"F0.wireOp",EDGE,"E0.top"),sQuery(id+"F0.wireOp",EDGE,"E0.left")])]});
            var Q11;
            Q11=makeQuery(id+"F3.opExtrude","SWEPT_EDGE",EDGE,{"disambiguationData":[OSD([sQuery(id+"F0.wireOp",EDGE,"E0.top"),sQuery(id+"F0.wireOp",EDGE,"E0.right")])]});
            var Q12;
            {var subQ0=sQuery(id+"F7.wireOp",EDGE,"E121.MirrorCS");var subQ1=sQuery(id+"F7.wireOp",EDGE,"E119.MirrorCS");Q12=makeQuery(id+"F9.boolean.opBoolean","MERGE",EDGE,{"derivedFrom":[makeQuery(id+"F8.opExtrude","SWEPT_EDGE",EDGE,{"disambiguationData":[OSD([subQ1,subQ0])]}),makeQuery(id+"F9.opExtrude","SWEPT_EDGE",EDGE,{"disambiguationData":[OSD([subQ1,subQ0])]})]});}
            var Q13;
            {var subQ0=sQuery(id+"F7.wireOp",EDGE,"E120.MirrorCS");var subQ1=sQuery(id+"F7.wireOp",EDGE,"E119.MirrorCS");Q13=makeQuery(id+"F9.boolean.opBoolean","MERGE",EDGE,{"derivedFrom":[makeQuery(id+"F8.opExtrude","SWEPT_EDGE",EDGE,{"disambiguationData":[OSD([subQ1,subQ0])]}),makeQuery(id+"F9.opExtrude","SWEPT_EDGE",EDGE,{"disambiguationData":[OSD([subQ1,subQ0])]})]});}
            var Q14;
            {var subQ0=sQuery(id+"F7.wireOp",EDGE,"E90.0");var subQ1=sQuery(id+"F7.wireOp",EDGE,"E88.0");Q14=makeQuery(id+"F9.boolean.opBoolean","MERGE",EDGE,{"derivedFrom":[makeQuery(id+"F8.opExtrude","SWEPT_EDGE",EDGE,{"disambiguationData":[OSD([subQ1,subQ0])]}),makeQuery(id+"F9.opExtrude","SWEPT_EDGE",EDGE,{"disambiguationData":[OSD([subQ1,subQ0])]})]});}
            var Q15;
            {var subQ0=sQuery(id+"F7.wireOp",EDGE,"E90.0");var subQ1=sQuery(id+"F7.wireOp",EDGE,"E89.0");Q15=makeQuery(id+"F9.boolean.opBoolean","MERGE",EDGE,{"derivedFrom":[makeQuery(id+"F8.opExtrude","SWEPT_EDGE",EDGE,{"disambiguationData":[OSD([subQ1,subQ0])]}),makeQuery(id+"F9.opExtrude","SWEPT_EDGE",EDGE,{"disambiguationData":[OSD([subQ1,subQ0])]})]});}
            var Q16;
            Q16=makeQuery(id+"F10.opExtrude","CAP_EDGE",EDGE,{"disambiguationData":[OSD([sQuery(id+"F7.wireOp",EDGE,"E85.0")])],"isStart":true});
            var Q17;
            Q17=makeQuery(id+"F10.opExtrude","SWEPT_EDGE",EDGE,{"disambiguationData":[OSD([sQuery(id+"F7.wireOp",EDGE,"E85.0"),sQuery(id+"F7.wireOp",EDGE,"E128.right")])]});
            var Q18;
            Q18=makeQuery(id+"F10.opExtrude","SWEPT_EDGE",EDGE,{"disambiguationData":[OSD([sQuery(id+"F7.wireOp",EDGE,"E85.0"),sQuery(id+"F7.wireOp",EDGE,"E128.left")])]});
            var Q19;
            Q19=makeQuery(id+"F10.opExtrude","CAP_EDGE",EDGE,{"disambiguationData":[OSD([sQuery(id+"F7.wireOp",EDGE,"E128.right")])],"isStart":true});
            var Q20;
            Q20=makeQuery(id+"F10.opExtrude","CAP_EDGE",EDGE,{"disambiguationData":[OSD([sQuery(id+"F7.wireOp",EDGE,"E128.bottom")])],"isStart":true});
            var Q21;
            Q21=makeQuery(id+"F10.opExtrude","SWEPT_EDGE",EDGE,{"disambiguationData":[OSD([sQuery(id+"F7.wireOp",EDGE,"E128.bottom"),sQuery(id+"F7.wireOp",EDGE,"E128.right")])]});
            var Q22;
            Q22=makeQuery(id+"F10.opExtrude","CAP_EDGE",EDGE,{"disambiguationData":[OSD([sQuery(id+"F7.wireOp",EDGE,"E128.left")])],"isStart":true});
            var Q23;
            Q23=makeQuery(id+"F10.opExtrude","SWEPT_EDGE",EDGE,{"disambiguationData":[OSD([sQuery(id+"F7.wireOp",EDGE,"E128.bottom"),sQuery(id+"F7.wireOp",EDGE,"E128.left")])]});
            fillet(context, id + "F13", {"entities" : qUnion([Q0, Q1, Q2, Q3, Q4, Q5, Q6, Q7, Q8, Q9, Q10, Q11, Q12, Q13, Q14, Q15, Q16, Q17, Q18, Q19, Q20, Q21, Q22, Q23]), "radius" : 2 * mm, "tangentPropagation" : true, "allowEdgeOverflow" : false});
        }
    });
